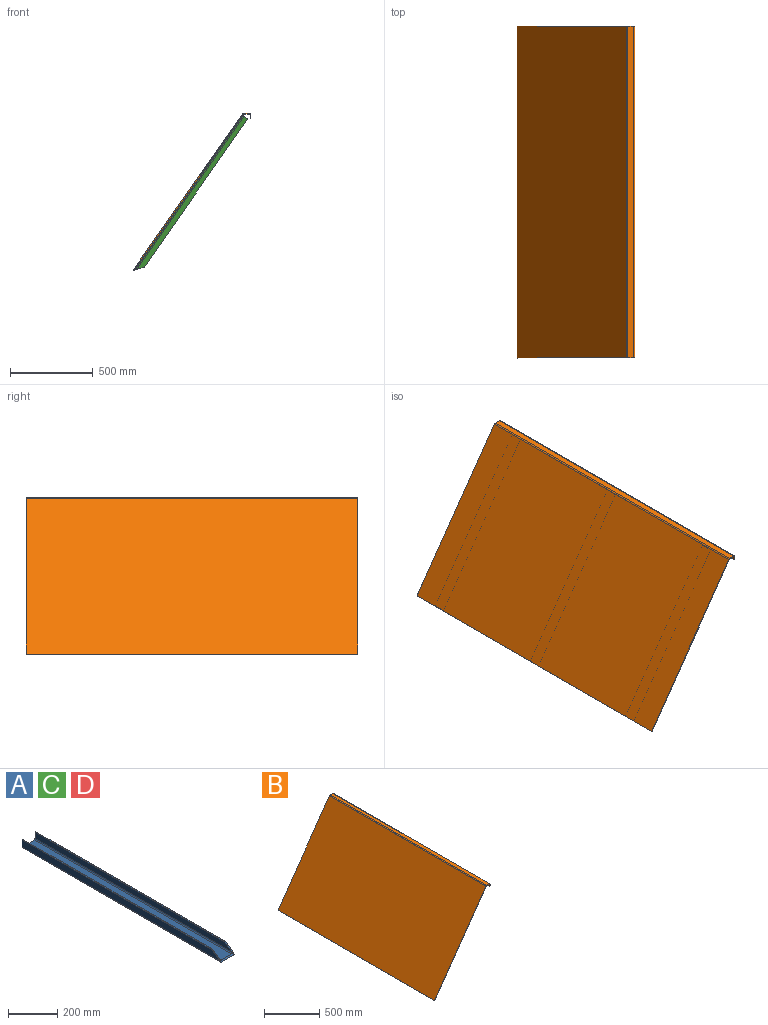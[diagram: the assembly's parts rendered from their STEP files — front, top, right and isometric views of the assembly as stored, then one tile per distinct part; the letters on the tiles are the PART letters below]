
ASSEMBLY  parts=4 mates=3
PART A: 14 faces, bbox 80x1140x40 mm
  f0: plane 1090x5mm, normal (0,0,1), area 5450mm2, adj f3,f4,f7,f13
  f1: plane 1090x5mm, normal (0,0,1), area 5450mm2, adj f4,f5,f8,f13
  f2: plane 1133.75x60mm, normal (0,0,1), area 68025mm2, adj f4,f9,f10,f13
  f3: plane 1133.75x35mm, normal (1,0,0), area 38915.6mm2, adj f0,f4,f12,f13
  f4: plane 80x40mm, normal (0,1,0), area 750mm2, adj f0,f1,f2,f3,f5,f6,f7,f8
  f5: plane 1133.75x35mm, normal (-1,0,0), area 38915.6mm2, adj f1,f4,f11,f13
  f6: plane 1140x70mm, normal (0,0,-1), area 79800mm2, adj f4,f11,f12,f13
  f7: plane 1127.5x30mm, normal (-1,0,0), area 33262.5mm2, adj f0,f4,f10,f13
  f8: plane 1127.5x30mm, normal (1,0,0), area 33262.5mm2, adj f1,f4,f9,f13
  f9: cylinder r=5mm len=1133.75mm, axis (0,1,0), area 8886.6mm2, adj f2,f4,f8,f13
  f10: cylinder r=5mm len=1133.75mm, axis (0,-1,0), area 8886.6mm2, adj f2,f4,f7,f13
  f11: cylinder r=5mm len=1140mm, axis (0,-1,0), area 8935.7mm2, adj f4,f5,f6,f13
  f12: cylinder r=5mm len=1140mm, axis (0,1,0), area 8935.7mm2, adj f3,f4,f6,f13
  f13: plane 80x50mm, normal (0,-0.62,0.78), area 1200.6mm2, adj f0,f1,f2,f3,f5,f6,f7,f8
PART B: 22 faces, bbox 711x2000x946.9 mm
  f0: plane 942.68x662.16mm, normal (0,1,0), area 5736.5mm2, adj f1,f3,f4,f19
  f1: plane 2000x4.1mm, normal (-0.57,0,-0.82), area 10000mm2, adj f0,f2,f3,f4
  f2: plane 942.68x662.16mm, normal (0,-1,0), area 5736.5mm2, adj f1,f3,f4,f18
  f3: plane 2000x939.81mm, normal (-0.82,0,0.57), area 2294588.7mm2, adj f0,f1,f2,f20
  f4: plane 2000x939.81mm, normal (0.82,0,-0.57), area 2294588.7mm2, adj f0,f1,f2,f21
  f5: plane 34.79x5mm, normal (0,1,0), area 174mm2, adj f7,f8,f14,f19
  f6: plane 34.79x5mm, normal (0,-1,0), area 174mm2, adj f7,f8,f15,f18
  f7: plane 2000x34.79mm, normal (0,0,1), area 69588.7mm2, adj f5,f6,f16,f20
  f8: plane 2000x34.79mm, normal (0,0,-1), area 69588.7mm2, adj f5,f6,f17,f21
  f9: plane 2000x5mm, normal (0,0,-1), area 10000mm2, adj f10,f11,f12,f13
  f10: plane 20x5mm, normal (0,1,0), area 100mm2, adj f9,f12,f13,f14
  f11: plane 20x5mm, normal (0,-1,0), area 100mm2, adj f9,f12,f13,f15
  f12: plane 2000x20mm, normal (1,0,0), area 40000mm2, adj f9,f10,f11,f16
  f13: plane 2000x20mm, normal (-1,0,0), area 40000mm2, adj f9,f10,f11,f17
  f14: plane 10x10mm, normal (0,1,0), area 58.9mm2, adj f5,f10,f16,f17
  f15: plane 10x10mm, normal (0,-1,0), area 58.9mm2, adj f6,f11,f16,f17
  f16: cylinder r=10mm len=2000mm, axis (0,1,0), area 31415.9mm2, adj f7,f12,f14,f15
  f17: cylinder r=5mm len=2000mm, axis (0,1,0), area 15708mm2, adj f8,f13,f14,f15
  f18: plane 8.19x7.13mm, normal (0,-1,0), area 36mm2, adj f2,f6,f20,f21
  f19: plane 8.19x7.13mm, normal (0,1,0), area 36mm2, adj f0,f5,f20,f21
  f20: cylinder r=10mm len=2000mm, axis (0,-1,0), area 19198.6mm2, adj f3,f7,f18,f19
  f21: cylinder r=5mm len=2000mm, axis (0,-1,0), area 9599.3mm2, adj f4,f8,f18,f19
PART C: same geometry as A
PART D: same geometry as A
PLACE A rot(axis=(0.66,0.66,0.35),141.9deg) t=(-195.69,39.65,205.99)mm
PLACE B t=(-270.81,39.65,-261.05)mm fixed
PLACE C rot(axis=(0.66,0.66,0.35),141.9deg) t=(-195.69,-772.35,205.99)mm
PLACE D rot(axis=(0.66,0.66,0.35),141.9deg) t=(-195.69,851.65,205.99)mm
MATE fastened C.f6 <-> B.f4  axis (-0.82,0,0.57) through (-195.69,-772.35,205.99)mm
MATE fastened D.f6 <-> B.f4  axis (-0.82,0,0.57) through (-195.69,851.65,205.99)mm
MATE fastened A.f6 <-> B.f4  axis (-0.82,0,0.57) through (-195.69,39.65,205.99)mm
